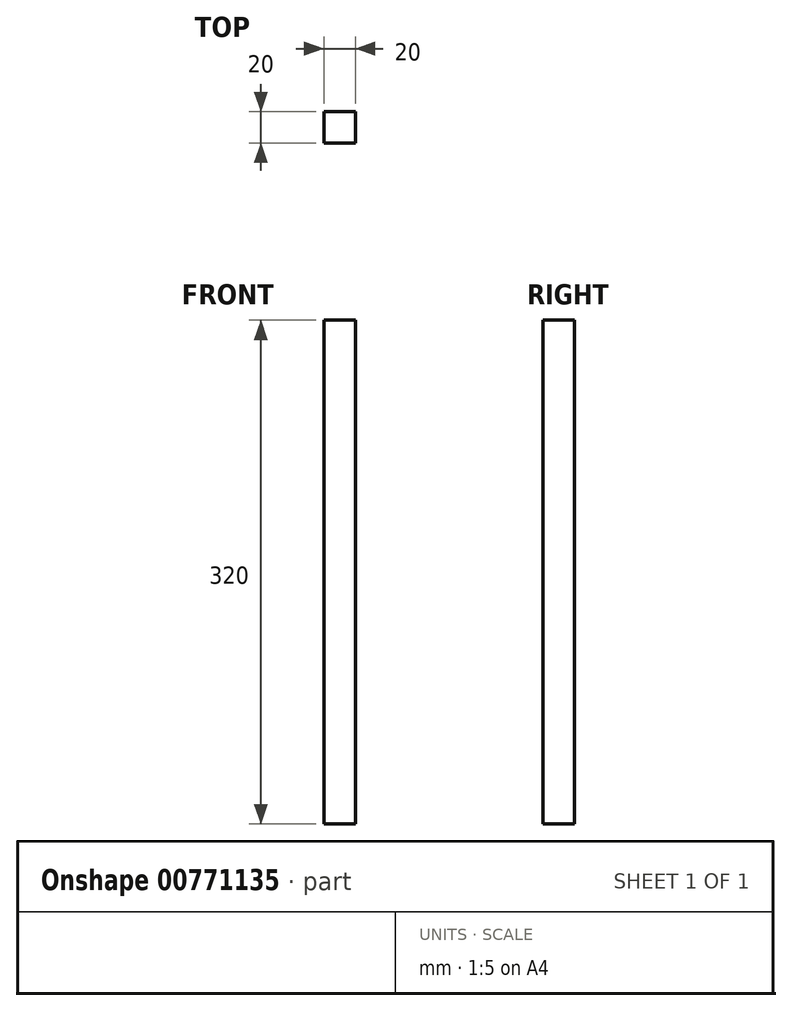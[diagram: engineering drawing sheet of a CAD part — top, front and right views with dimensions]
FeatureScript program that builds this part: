
annotation { "Feature Type Name" : "Feature", "Feature Type Description" : "" }
export const myFeature = defineFeature(function(context is Context, id is Id, definition is map)
    precondition{}
    {
        {
            var Q0;
            Q0=qCreatedBy(makeId("Top.planeOp"),FACE);
            var sketch = newSketch(context, id + "F0", { "sketchPlane" : qUnion([Q0])});
            skLineSegment(sketch, "E0.bottom", {"start": v(10, -10) * mm, "end": v(-10, -10) * mm});
            skLineSegment(sketch, "E0.top", {"start": v(10, 10) * mm, "end": v(-10, 10) * mm});
            skLineSegment(sketch, "E0.left", {"start": v(10, -10) * mm, "end": v(10, 10) * mm});
            skLineSegment(sketch, "E0.right", {"start": v(-10, -10) * mm, "end": v(-10, 10) * mm});
            skPoint(sketch, "E0.middle", {"position": v(0, 0) * mm});
            skSolve(sketch);
        }
        {
            var Q0;
            Q0 = qSketchRegion(id + "F0", true);
            extrude(context, id + "F1", {"entities" : qUnion([Q0]), "depth" : 320 * mm, "offsetDistance" : 25 * mm});
        }
    });
